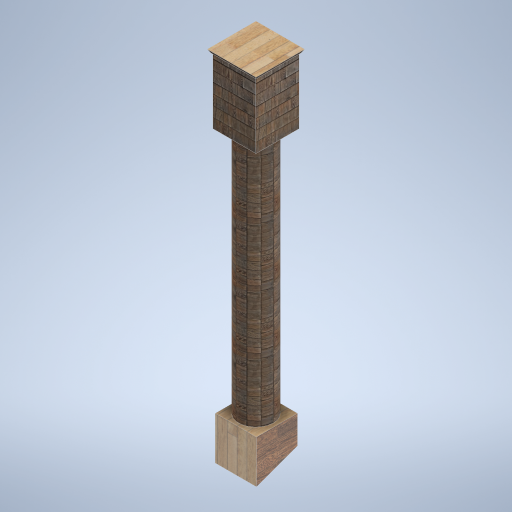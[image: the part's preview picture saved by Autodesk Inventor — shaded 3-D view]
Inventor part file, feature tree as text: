
AUTODESK INVENTOR PART (.ipt)
format: ipt  version: 2024.2 (Build 282272000, 272)  size: 352,768 bytes
history: native  units: in
note: dims shown in document units (in); Inventor stores cm internally (conversion verified against a paired STEP export)
features: sketch x5, other x3, plane x1
ambient origin geometry x8: Origin, YZ Plane, XZ Plane, XY Plane, X Axis, Y Axis, Z Axis, Center Point
bodies: Solid1 (feature_tree)
feature tree (9):
  other  "side_pillar_01.ipt"
  other  "Solid1::side_pillar_01.ipt"
  other  "TaggingFeature1"
  sketch  "Sketch1"  dims[d0=0.3937in]
  sketch  "Sketch2"
  sketch  "Sketch3"
  sketch  "Sketch4"
  sketch  "Sketch5"
  plane  "Work Plane3"
